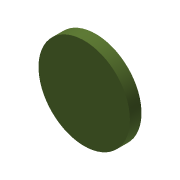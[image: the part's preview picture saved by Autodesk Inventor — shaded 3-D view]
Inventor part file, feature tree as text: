
AUTODESK INVENTOR PART (.ipt)
format: ipt  version: 2014 (Build 180170000, 170)  size: 82,944 bytes
history: native  units: mm
features: extrude x2, sketch x2
ambient origin geometry x8: Origin, YZ Plane, XZ Plane, XY Plane, X Axis, Y Axis, Z Axis, Center Point
bodies: Solid1 (feature_tree)
feature tree (4):
  extrude  "Extrusion1"  Depth=4.0mm
  extrude  "Extrusion2"  Depth=4.0mm TaperAngle=0.0deg
  sketch  "Sketch1"  dims[d0=150.0mm d1=4.0mm]
  sketch  "Sketch2"  dims[d2=15.0mm d3=0.0mm d4=4.0mm d5=0.0mm]
